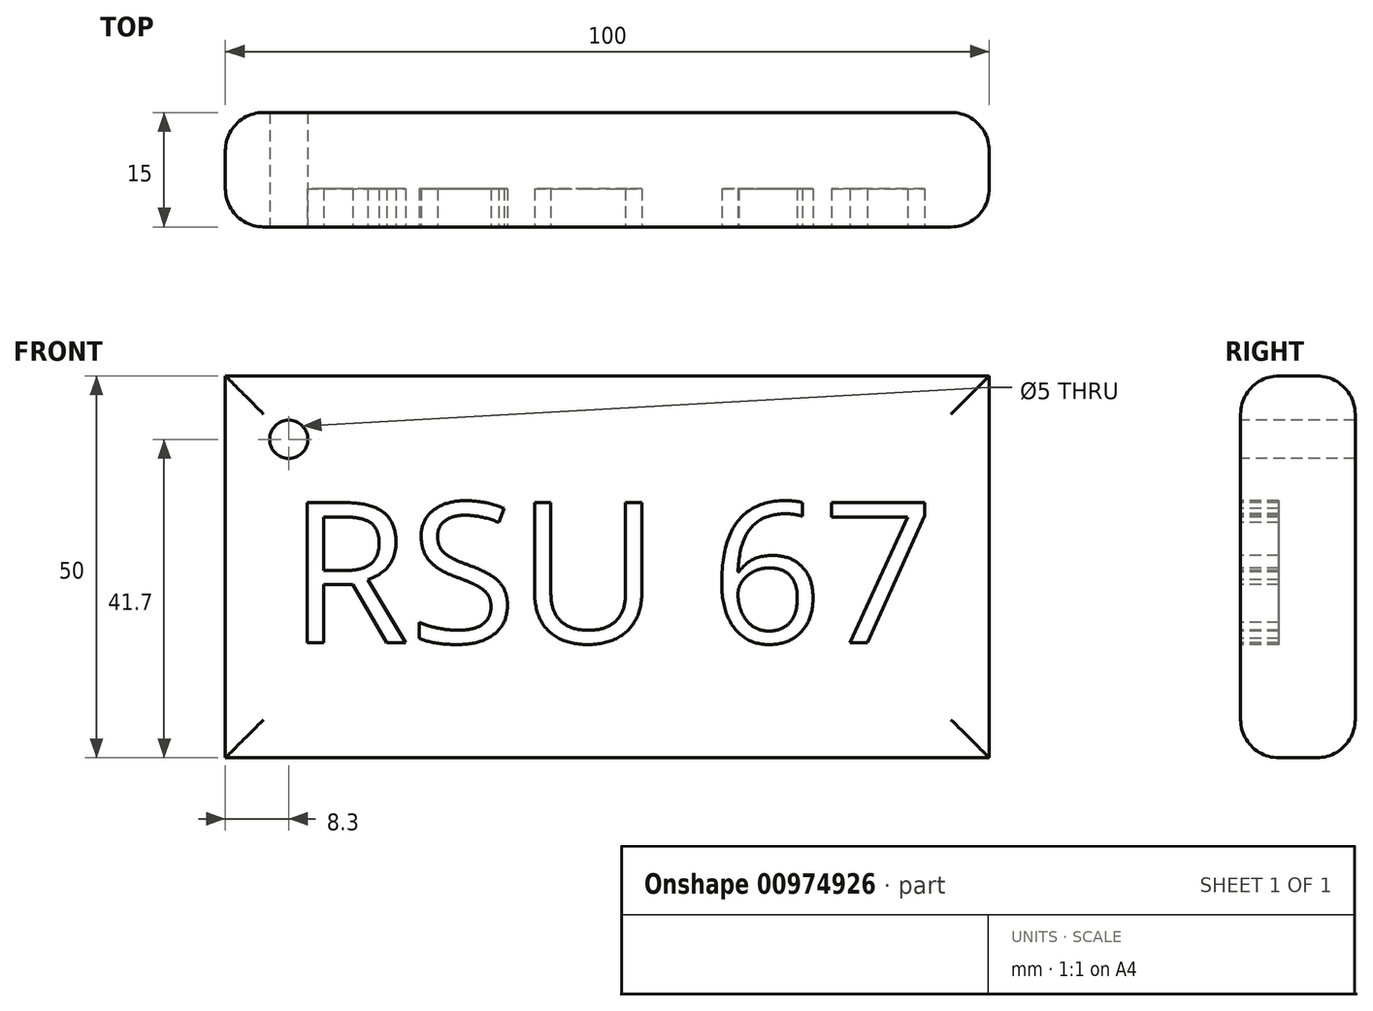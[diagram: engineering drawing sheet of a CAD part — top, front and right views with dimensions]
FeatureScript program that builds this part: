
annotation { "Feature Type Name" : "Feature", "Feature Type Description" : "" }
export const myFeature = defineFeature(function(context is Context, id is Id, definition is map)
    precondition{}
    {
        {
            var Q0;
            Q0=qCreatedBy(makeId("Front.planeOp"),FACE);
            var sketch = newSketch(context, id + "F0", { "sketchPlane" : qUnion([Q0])});
            skLineSegment(sketch, "E0.bottom", {"start": v(50, 25) * mm, "end": v(-50, 25) * mm});
            skLineSegment(sketch, "E0.top", {"start": v(50, -25) * mm, "end": v(-50, -25) * mm});
            skLineSegment(sketch, "E0.left", {"start": v(50, 25) * mm, "end": v(50, -25) * mm});
            skLineSegment(sketch, "E0.right", {"start": v(-50, 25) * mm, "end": v(-50, -25) * mm});
            skPoint(sketch, "E0.middle", {"position": v(0, 0) * mm});
            skSolve(sketch);
        }
        {
            var Q0;
            Q0 = qSketchRegion(id + "F0", true);
            extrude(context, id + "F1", {"entities" : qUnion([Q0]), "depth" : 15 * mm, "offsetDistance" : 25 * mm});
        }
        {
            var Q0;
            Q0=makeQuery(id+"F1.opExtrude","CAP_EDGE",EDGE,{"disambiguationData":[OSD([sQuery(id+"F0.wireOp",EDGE,"E0.bottom")])],"isStart":false});
            var Q1;
            Q1=makeQuery(id+"F1.opExtrude","CAP_EDGE",EDGE,{"disambiguationData":[OSD([sQuery(id+"F0.wireOp",EDGE,"E0.left")])],"isStart":false});
            var Q2;
            Q2=makeQuery(id+"F1.opExtrude","CAP_EDGE",EDGE,{"disambiguationData":[OSD([sQuery(id+"F0.wireOp",EDGE,"E0.top")])],"isStart":false});
            var Q3;
            Q3=makeQuery(id+"F1.opExtrude","CAP_EDGE",EDGE,{"disambiguationData":[OSD([sQuery(id+"F0.wireOp",EDGE,"E0.right")])],"isStart":false});
            var Q4;
            Q4=makeQuery(id+"F1.opExtrude","CAP_EDGE",EDGE,{"disambiguationData":[OSD([sQuery(id+"F0.wireOp",EDGE,"E0.bottom")])],"isStart":true});
            var Q5;
            Q5=makeQuery(id+"F1.opExtrude","CAP_EDGE",EDGE,{"disambiguationData":[OSD([sQuery(id+"F0.wireOp",EDGE,"E0.right")])],"isStart":true});
            var Q6;
            Q6=makeQuery(id+"F1.opExtrude","CAP_EDGE",EDGE,{"disambiguationData":[OSD([sQuery(id+"F0.wireOp",EDGE,"E0.top")])],"isStart":true});
            var Q7;
            Q7=makeQuery(id+"F1.opExtrude","CAP_EDGE",EDGE,{"disambiguationData":[OSD([sQuery(id+"F0.wireOp",EDGE,"E0.left")])],"isStart":true});
            fillet(context, id + "F2", {"entities" : qUnion([Q0, Q1, Q2, Q3, Q4, Q5, Q6, Q7]), "radius" : 5 * mm, "tangentPropagation" : true, "allowEdgeOverflow" : false});
        }
        {
            var Q0;
            {var subQ0=sQuery(id+"F0.wireOp",EDGE,"E0.left");var subQ1=sQuery(id+"F0.wireOp",EDGE,"E0.top");var subQ2=sQuery(id+"F0.wireOp",EDGE,"E0.bottom");var subQ3=sQuery(id+"F0.wireOp",EDGE,"E0.right");Q0=makeQuery(id+"FsGq3vIgySG3jhu_1.boolean.opBoolean","SPLIT",FACE,{"disambiguationData":[TD([makeQuery(id+"FsGq3vIgySG3jhu_1.opExtrude","SWEPT_FACE",FACE,{"disambiguationData":[OSD([sQuery(id+"FZypedSFBnDjyIB_1.wireOp",EDGE,"9cf931ec-50e4-4600-a80b-8a58a7e66966.sketch_text.stroke-0")])]})])],"derivedFrom":makeQuery(id+"F1.opExtrude","CAP_FACE",FACE,{"disambiguationData":[OSD([subQ2,subQ1,subQ0,subQ3])],"isStart":false})});}
            var sketch = newSketch(context, id + "F3", { "sketchPlane" : qUnion([Q0])});
            skCircle(sketch, "E1", {"center": v(-41.7, 16.7) * mm, "radius": 2.5 * mm});
            skSolve(sketch);
        }
        {
            var Q0;
            Q0 = qSketchRegion(id + "F3", true);
            extrude(context, id + "F4", {"entities" : qUnion([Q0]), "operationType" : NewBodyOperationType.REMOVE, "endBound" : BoundingType.THROUGH_ALL, "oppositeDirection" : true, "depth" : 25 * mm, "offsetDistance" : 25 * mm});
        }
        {
            var Q0;
            Q0=makeQuery(id+"F1.opExtrude","CAP_FACE",FACE,{"disambiguationData":[OSD([sQuery(id+"F0.wireOp",EDGE,"E0.bottom"),sQuery(id+"F0.wireOp",EDGE,"E0.top"),sQuery(id+"F0.wireOp",EDGE,"E0.left"),sQuery(id+"F0.wireOp",EDGE,"E0.right")])],"isStart":false});
            var sketch = newSketch(context, id + "F5", { "sketchPlane" : qUnion([Q0])});
            skText(sketch, "E2", { "text": "RSU 67", "fontName": "OpenSans-Regular.ttf"});
            const initialGuessF5  = {"E2": [-0.0418, -0.00992, 1, 0, 0.01848]};
            skSetInitialGuess(sketch, initialGuessF5);
            skSolve(sketch);
        }
        {
            var Q0;
            Q0 = qSketchRegion(id + "F5", true);
            extrude(context, id + "F6", {"entities" : qUnion([Q0]), "operationType" : NewBodyOperationType.REMOVE, "oppositeDirection" : true, "depth" : 5 * mm, "offsetDistance" : 25 * mm});
        }
    });
